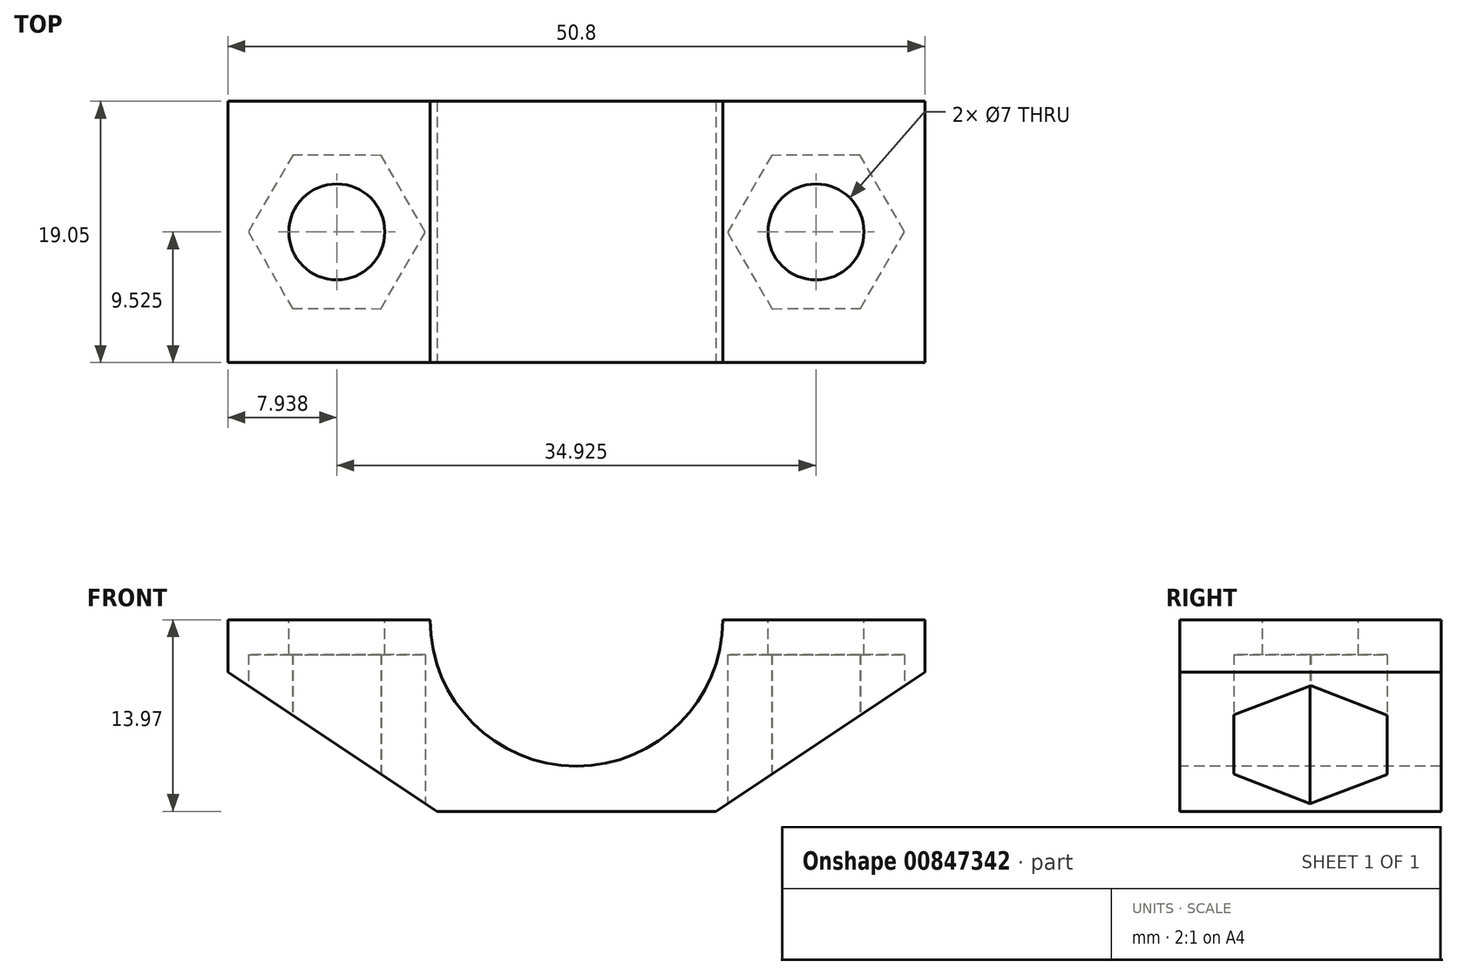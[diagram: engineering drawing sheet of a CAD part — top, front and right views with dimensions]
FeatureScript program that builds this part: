
annotation { "Feature Type Name" : "Feature", "Feature Type Description" : "" }
export const myFeature = defineFeature(function(context is Context, id is Id, definition is map)
    precondition{}
    {
        {
            var Q0;
            Q0=qCreatedBy(makeId("Front.planeOp"),FACE);
            var sketch = newSketch(context, id + "F0", { "sketchPlane" : qUnion([Q0])});
            skLineSegment(sketch, "E0.bottom", {"start": v(25.4, -13.97) * mm, "end": v(-25.4, -13.97) * mm});
            skLineSegment(sketch, "E0.top", {"start": v(25.4, 0) * mm, "end": v(-25.4, 0) * mm});
            skLineSegment(sketch, "E0.left", {"start": v(25.4, -13.97) * mm, "end": v(25.4, 0) * mm});
            skLineSegment(sketch, "E0.right", {"start": v(-25.4, -13.97) * mm, "end": v(-25.4, 0) * mm});
            skPoint(sketch, "E0.middle", {"position": v(-35.35, 0) * mm});
            skPoint(sketch, "E1", {"position": v(0, 0) * mm});
            skSolve(sketch);
        }
        {
            var Q0;
            Q0=qSketchRegion(id+"F0",true);
            extrude(context, id + "F1", {"entities" : qUnion([Q0]), "oppositeDirection" : true, "depth" : 19.05 * mm, "offsetDistance" : 25.4 * mm});
        }
        {
            var Q0;
            Q0=makeQuery(id+"F0.imprint","IMPRINT",FACE,{"disambiguationData":[TD([[makeQuery(id+"F0.imprint","IMPRINT",EDGE,{"derivedFrom":sQuery(id+"F0.wireOp",EDGE,"E0.bottom")}),-1.0]])]});
            var sketch = newSketch(context, id + "F2", { "sketchPlane" : qUnion([Q0])});
            skCircle(sketch, "E2", {"center": v(0, 0) * mm, "radius": 10.67 * mm});
            skSolve(sketch);
        }
        {
            var Q0;
            {var subQ0=sQuery(id+"F2.wireOp",EDGE,"E2");var subQ1=makeQuery(id+"F0.imprint","IMPRINT",EDGE,{"derivedFrom":sQuery(id+"F0.wireOp",EDGE,"E0.top")});var subQ2=makeQuery(id+"F2.imprint","INTERSECT",VERTEX,{"disambiguationData":[OD(0.0)],"derivedFrom":[subQ1,subQ0]});Q0=makeQuery(id+"F2.imprint","IMPRINT",FACE,{"disambiguationData":[TD([[makeQuery(id+"F2.imprint","IMPRINT",EDGE,{"disambiguationData":[TD([[subQ2,1.0]])],"derivedFrom":subQ0}),1.0]])]});}
            var Q1;
            Q1=sQuery(id+"F2.wireOp",EDGE,"E2");
            extrude(context, id + "F3", {"entities" : qUnion([Q0]), "operationType" : NewBodyOperationType.REMOVE, "surfaceEntities" : qUnion([Q1]), "oppositeDirection" : true, "depth" : 19.05 * mm, "offsetDistance" : 25.4 * mm});
        }
        {
            var Q0;
            Q0=makeQuery(id+"F1.opExtrude","CAP_FACE",FACE,{"disambiguationData":[OSD([sQuery(id+"F0.wireOp",EDGE,"E0.bottom"),sQuery(id+"F0.wireOp",EDGE,"E0.top"),sQuery(id+"F0.wireOp",EDGE,"E0.left"),sQuery(id+"F0.wireOp",EDGE,"E0.right")])],"isStart":true});
            var sketch = newSketch(context, id + "F4", { "sketchPlane" : qUnion([Q0])});
            skLineSegment(sketch, "E3", {"start": v(-25.4, -13.97) * mm, "end": v(-25.4, -3.81) * mm});
            skLineSegment(sketch, "E4", {"start": v(-25.4, -3.81) * mm, "end": v(-10.16, -13.97) * mm});
            skLineSegment(sketch, "E5", {"start": v(-10.16, -13.97) * mm, "end": v(-25.4, -13.97) * mm});
            skLineSegment(sketch, "E6.MirrorCS", {"start": v(25.4, -3.81) * mm, "end": v(10.16, -13.97) * mm});
            skLineSegment(sketch, "E7.MirrorCS", {"start": v(10.16, -13.97) * mm, "end": v(25.4, -13.97) * mm});
            skLineSegment(sketch, "E8.MirrorCS", {"start": v(25.4, -13.97) * mm, "end": v(25.4, -3.81) * mm});
            skPoint(sketch, "E9", {"position": v(0, -13.97) * mm});
            skSolve(sketch);
        }
        {
            var Q0;
            Q0=qSketchRegion(id+"F4",true);
            extrude(context, id + "F5", {"entities" : qUnion([Q0]), "operationType" : NewBodyOperationType.REMOVE, "oppositeDirection" : true, "depth" : 25.4 * mm, "offsetDistance" : 25.4 * mm});
        }
        {
            var Q0;
            {var subQ0=sQuery(id+"F0.wireOp",EDGE,"E0.right");var subQ2=sQuery(id+"F0.wireOp",EDGE,"E0.top");Q0=makeQuery(id+"F3.boolean.opBoolean","SPLIT",FACE,{"disambiguationData":[TD([makeQuery(id+"F1.opExtrude","SWEPT_FACE",FACE,{"disambiguationData":[OSD([subQ0])]})])],"derivedFrom":makeQuery(id+"F1.opExtrude","SWEPT_FACE",FACE,{"disambiguationData":[OSD([subQ2])]})});}
            var sketch = newSketch(context, id + "F6", { "sketchPlane" : qUnion([Q0])});
            skCircle(sketch, "E10", {"center": v(-17.46, 9.53) * mm, "radius": 3.5 * mm});
            skCircle(sketch, "E11.MirrorC", {"center": v(17.46, 9.53) * mm, "radius": 3.5 * mm});
            skSolve(sketch);
        }
        {
            var Q0;
            Q0=qSketchRegion(id+"F6",true);
            extrude(context, id + "F7", {"entities" : qUnion([Q0]), "operationType" : NewBodyOperationType.REMOVE, "oppositeDirection" : true, "depth" : 25.4 * mm, "offsetDistance" : 25.4 * mm});
        }
        {
            var Q0;
            Q0=makeQuery(id+"F1.opExtrude","SWEPT_FACE",FACE,{"disambiguationData":[OSD([sQuery(id+"F0.wireOp",EDGE,"E0.bottom")])]});
            var sketch = newSketch(context, id + "F8", { "sketchPlane" : qUnion([Q0])});
            skCircle(sketch, "E12.cCircle", {"center": v(-17.46, -9.53) * mm, "radius": 5.59 * mm, "construction": true});
            skLineSegment(sketch, "E12.0", {"start": v(-20.7, -3.95) * mm, "end": v(-14.25, -3.93) * mm});
            skLineSegment(sketch, "E12.1", {"start": v(-14.25, -3.93) * mm, "end": v(-11.01, -9.5) * mm});
            skLineSegment(sketch, "E12.2", {"start": v(-11.01, -9.5) * mm, "end": v(-14.22, -15.1) * mm});
            skLineSegment(sketch, "E12.3", {"start": v(-14.22, -15.1) * mm, "end": v(-20.67, -15.12) * mm});
            skLineSegment(sketch, "E12.4", {"start": v(-20.67, -15.12) * mm, "end": v(-23.91, -9.55) * mm});
            skLineSegment(sketch, "E12.5", {"start": v(-23.91, -9.55) * mm, "end": v(-20.7, -3.95) * mm});
            skPoint(sketch, "E12.0.midPoint", {"position": v(-17.48, -3.94) * mm});
            skLineSegment(sketch, "E13.MirrorCS", {"start": v(20.7, -3.95) * mm, "end": v(14.25, -3.93) * mm});
            skLineSegment(sketch, "E14.MirrorCS", {"start": v(14.25, -3.93) * mm, "end": v(11.01, -9.5) * mm});
            skLineSegment(sketch, "E15.MirrorCS", {"start": v(11.01, -9.5) * mm, "end": v(14.22, -15.1) * mm});
            skLineSegment(sketch, "E16.MirrorCS", {"start": v(14.22, -15.1) * mm, "end": v(20.67, -15.12) * mm});
            skLineSegment(sketch, "E17.MirrorCS", {"start": v(20.67, -15.12) * mm, "end": v(23.91, -9.55) * mm});
            skLineSegment(sketch, "E18.MirrorCS", {"start": v(23.91, -9.55) * mm, "end": v(20.7, -3.95) * mm});
            skSolve(sketch);
        }
        {
            var Q0;
            Q0 = qSketchRegion(id + "F8", true);
            extrude(context, id + "F9", {"entities" : qUnion([Q0]), "operationType" : NewBodyOperationType.REMOVE, "oppositeDirection" : true, "depth" : 11.43 * mm, "offsetDistance" : 25.4 * mm});
        }
    });
